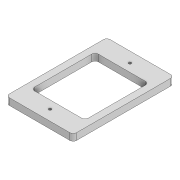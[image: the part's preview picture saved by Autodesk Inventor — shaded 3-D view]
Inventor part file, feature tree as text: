
AUTODESK INVENTOR PART (.ipt)
format: ipt  version: 2020 (Build 240168000, 168)  size: 111,616 bytes
history: native  units: mm
features: extrude x2, fillet x2, sketch x2
ambient origin geometry x8: Origin, YZ Plane, XZ Plane, XY Plane, X Axis, Y Axis, Z Axis, Center Point
bodies: Solid1 (feature_tree)
feature tree (6):
  extrude  "Extrusion1"  Depth=100.0mm
  fillet  "Fillet1"  Radius=59.5mm
  extrude  "Extrusion2"  Depth=10.0mm TaperAngle=0.0deg
  fillet  "Fillet2"  Radius=5.0mm
  sketch  "Sketch1"  dims[d0=150.0mm d1=100.0mm d2=59.5mm]
  sketch  "Sketch2"  dims[d3=4.0mm d4=10.0mm d5=0.0mm d6=5.0mm d7=95.0mm d8=80.0mm d9=10.0mm d10=0.0mm d11=5.0mm]
